# Revit family: P210876JX-025_JMW2427IL
name_source: partatom
category: Specialty Equipment
units: mm (PartAtom-declared; Revit-internal decimal feet)

## family parameters
Always vertical = Yes
Cut with Voids When Loaded = No
Enable Cutting in Views = No
Maintain Annotation Orientation = No
Part Type = Normal
Room Calculation Point = No
Round Connector Dimension = Use Diameter
Shared = No
Work Plane-Based = No

## types (1)
- JMW2427IL
    Apparent Load = 0 VA
    Body Material = ARCAT - Metal - Steel - Stainless
    Clearance Material = ARCAT - Clearance
    Default Elevation = 0"
    Depth = 23 1/4"
    Description = RISE™ 27" Microwave/Wall Oven with MultiMode® Convection System
Four à micro-ondes/mural RISE™ avec système de convection MultiMode®, 27 po
    Dimension Guide = https://access.whirlpool.com Guide&sku=JMW2427IL&language=EN
https://access.whirlpool.com Guide&sku=JMW2427IL&language=EN
    Display Panel Material = ARCAT - Glass - Black
    Door Front Panel Material = ARCAT - Metal - Steel - Stainless
    Door Material = ARCAT - Metal - Steel - Stainless
    Family Name = Combination Built-In Oven
    Feature 1 = Irresistible Interior
Intérieur irrésistible
    Feature 2 = 4.3-Inch Full Color LCD Display
Affichage en couleur ACL de 4,3 po
    Feature 3 = Cinematic Lighting
Éclairage cinématique
    Glass Material = ARCAT - Glass - Tempered - Black
    Handle Material = ARCAT - Metal - Steel - Grey
    Height = 43 3/4"
    Installation-Fabrication = https://access.whirlpool.com Instruction&sku=JMW2427IL&language=EN
https://access.whirlpool.com Instruction&sku=JMW2427IL&language=EN
    Manufacturer = JennAir
    Model = JMW2427IL
    Voltage = 0 V
    Width = 27"

## geometry (parser evidence)
native form markers: Sweep x5
no freeform markers — native parametric forms only
